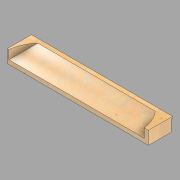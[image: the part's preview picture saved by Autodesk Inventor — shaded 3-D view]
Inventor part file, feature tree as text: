
AUTODESK INVENTOR PART (.ipt)
format: ipt  version: 2022.2 (Build 262287010, 287A)  size: 139,776 bytes
history: native  units: in
note: dims shown in document units (in); Inventor stores cm internally (conversion verified against a paired STEP export)
features: revolve x2, direct_edit x1, other x1
ambient origin geometry x8: Origin, YZ Plane, XZ Plane, XY Plane, X Axis, Y Axis, Z Axis, Center Point
bodies: Solid1 (feature_tree)
feature tree (4):
  direct_edit  "Direct Edit1"
  other  "Head (L)"
  revolve  "Rotate1"  [1 undecoded]
  revolve  "Rotate2"  [1 undecoded]
note: 2 required parameter values undecoded (feature->parameter linkage not recoverable at this tier; creation-order binding heuristic only, values carry confidence <= 0.55)
